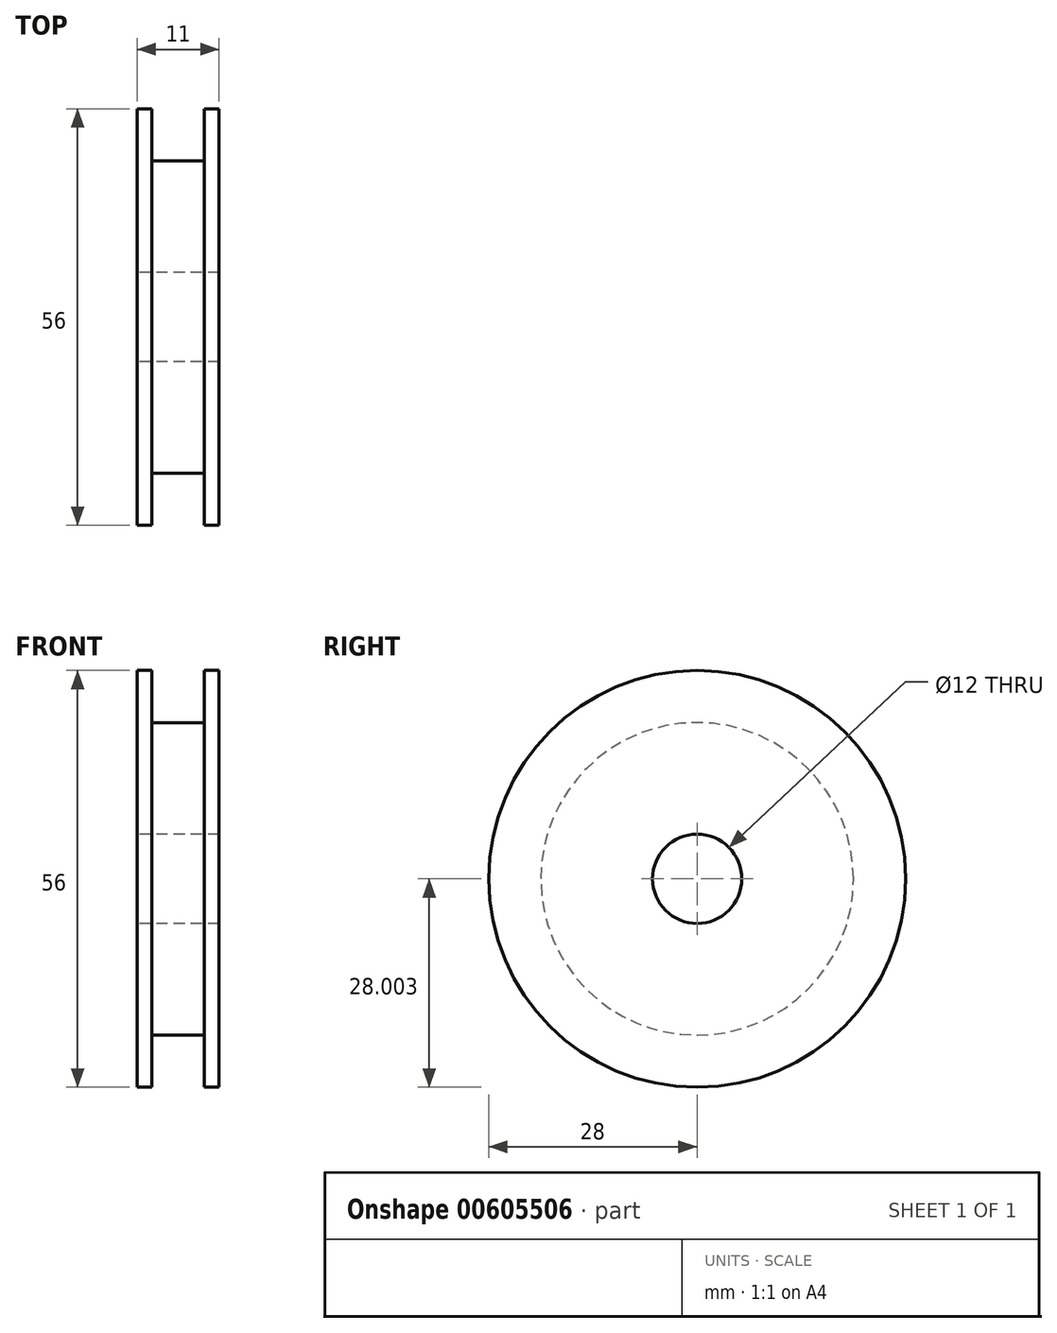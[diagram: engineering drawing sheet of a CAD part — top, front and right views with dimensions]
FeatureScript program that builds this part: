
annotation { "Feature Type Name" : "Feature", "Feature Type Description" : "" }
export const myFeature = defineFeature(function(context is Context, id is Id, definition is map)
    precondition{}
    {
        {
            var Q0;
            Q0=qCreatedBy(makeId("Front.planeOp"),FACE);
            var sketch = newSketch(context, id + "F0", { "sketchPlane" : qUnion([Q0])});
            skLineSegment(sketch, "E0.bottom", {"start": v(-9, 32.28) * mm, "end": v(-7, 32.28) * mm});
            skLineSegment(sketch, "E0.top", {"start": v(-9, 10.28) * mm, "end": v(-7, 10.28) * mm});
            skLineSegment(sketch, "E0.left", {"start": v(-9, 32.28) * mm, "end": v(-9, 10.28) * mm});
            skLineSegment(sketch, "E0.right", {"start": v(-7, 32.28) * mm, "end": v(-7, 10.28) * mm});
            skLineSegment(sketch, "E1.bottom", {"start": v(-7, 10.28) * mm, "end": v(0, 10.28) * mm});
            skLineSegment(sketch, "E1.top", {"start": v(-7, 25.28) * mm, "end": v(0, 25.28) * mm});
            skLineSegment(sketch, "E1.left", {"start": v(-7, 10.28) * mm, "end": v(-7, 25.28) * mm});
            skLineSegment(sketch, "E1.right", {"start": v(0, 10.28) * mm, "end": v(0, 25.28) * mm});
            skLineSegment(sketch, "E2.bottom", {"start": v(0, 10.28) * mm, "end": v(2, 10.28) * mm});
            skLineSegment(sketch, "E2.top", {"start": v(0, 32.28) * mm, "end": v(2, 32.28) * mm});
            skLineSegment(sketch, "E2.left", {"start": v(0, 10.28) * mm, "end": v(0, 32.28) * mm});
            skLineSegment(sketch, "E2.right", {"start": v(2, 10.28) * mm, "end": v(2, 32.28) * mm});
            skLineSegment(sketch, "E3", {"start": v(-11.7, 4.28) * mm, "end": v(5, 4.28) * mm, "construction": true});
            skSolve(sketch);
        }
        {
            var Q0;
            {var subQ0=sQuery(id+"F0.wireOp",EDGE,"E1.bottom");Q0=makeQuery(id+"F0.imprint","IMPRINT",FACE,{"disambiguationData":[TD([[makeQuery(id+"F0.imprint","IMPRINT",EDGE,{"derivedFrom":subQ0}),1.0]])]});}
            var Q1;
            Q1=makeQuery(id+"F0.imprint","IMPRINT",FACE,{"disambiguationData":[TD([[makeQuery(id+"F0.imprint","IMPRINT",EDGE,{"derivedFrom":sQuery(id+"F0.wireOp",EDGE,"E0.bottom")}),-1.0]])]});
            var Q2;
            {var subQ3=sQuery(id+"F0.wireOp",EDGE,"E2.bottom");Q2=makeQuery(id+"F0.imprint","IMPRINT",FACE,{"disambiguationData":[TD([[makeQuery(id+"F0.imprint","IMPRINT",EDGE,{"derivedFrom":subQ3}),1.0]])]});}
            var Q3;
            Q3=sQuery(id+"F0.wireOp",EDGE,"E3");
            revolve(context, id + "F1", {"entities" : qUnion([Q0, Q1, Q2]), "axis" : qUnion([Q3]), "revolveType" : RevolveType.FULL});
        }
    });
